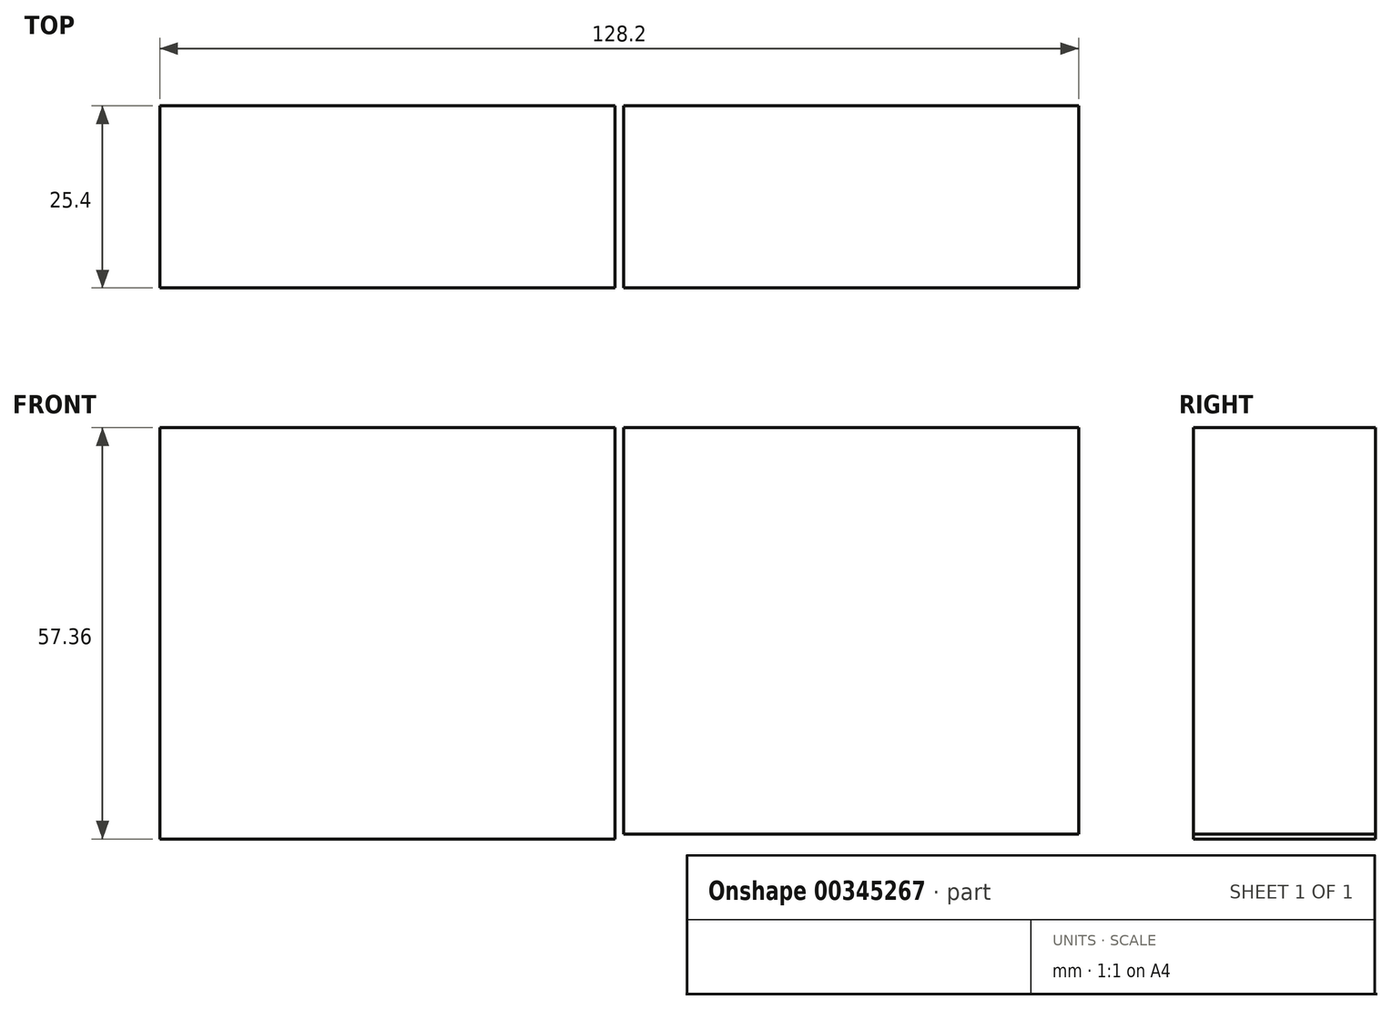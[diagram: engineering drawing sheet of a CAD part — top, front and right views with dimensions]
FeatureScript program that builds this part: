
annotation { "Feature Type Name" : "Feature", "Feature Type Description" : "" }
export const myFeature = defineFeature(function(context is Context, id is Id, definition is map)
    precondition{}
    {
        {
            var Q0;
            Q0=qCreatedBy(makeId("Front.planeOp"),FACE);
            var sketch = newSketch(context, id + "F0", { "sketchPlane" : qUnion([Q0])});
            skLineSegment(sketch, "E0.bottom", {"start": v(-61.26, 65.8) * mm, "end": v(2.24, 65.8) * mm});
            skLineSegment(sketch, "E0.top", {"start": v(-61.26, 8.44) * mm, "end": v(2.24, 8.44) * mm});
            skLineSegment(sketch, "E0.left", {"start": v(-61.26, 65.8) * mm, "end": v(-61.26, 8.44) * mm});
            skLineSegment(sketch, "E0.right", {"start": v(2.24, 65.8) * mm, "end": v(2.24, 8.44) * mm});
            skPoint(sketch, "E0.middle", {"position": v(-29.5, 37.12) * mm});
            skLineSegment(sketch, "E1.bottom", {"start": v(3.44, 65.8) * mm, "end": v(66.94, 65.8) * mm});
            skLineSegment(sketch, "E1.top", {"start": v(3.44, 9.12) * mm, "end": v(66.94, 9.12) * mm});
            skLineSegment(sketch, "E1.left", {"start": v(3.44, 65.8) * mm, "end": v(3.44, 9.12) * mm});
            skLineSegment(sketch, "E1.right", {"start": v(66.94, 65.8) * mm, "end": v(66.94, 9.12) * mm});
            skPoint(sketch, "E1.middle", {"position": v(35.19, 37.46) * mm});
            skSolve(sketch);
        }
        {
            var Q0;
            Q0 = qSketchRegion(id + "F0", true);
            extrude(context, id + "F1", {"entities" : qUnion([Q0]), "depth" : 25.4 * mm});
        }
    });
